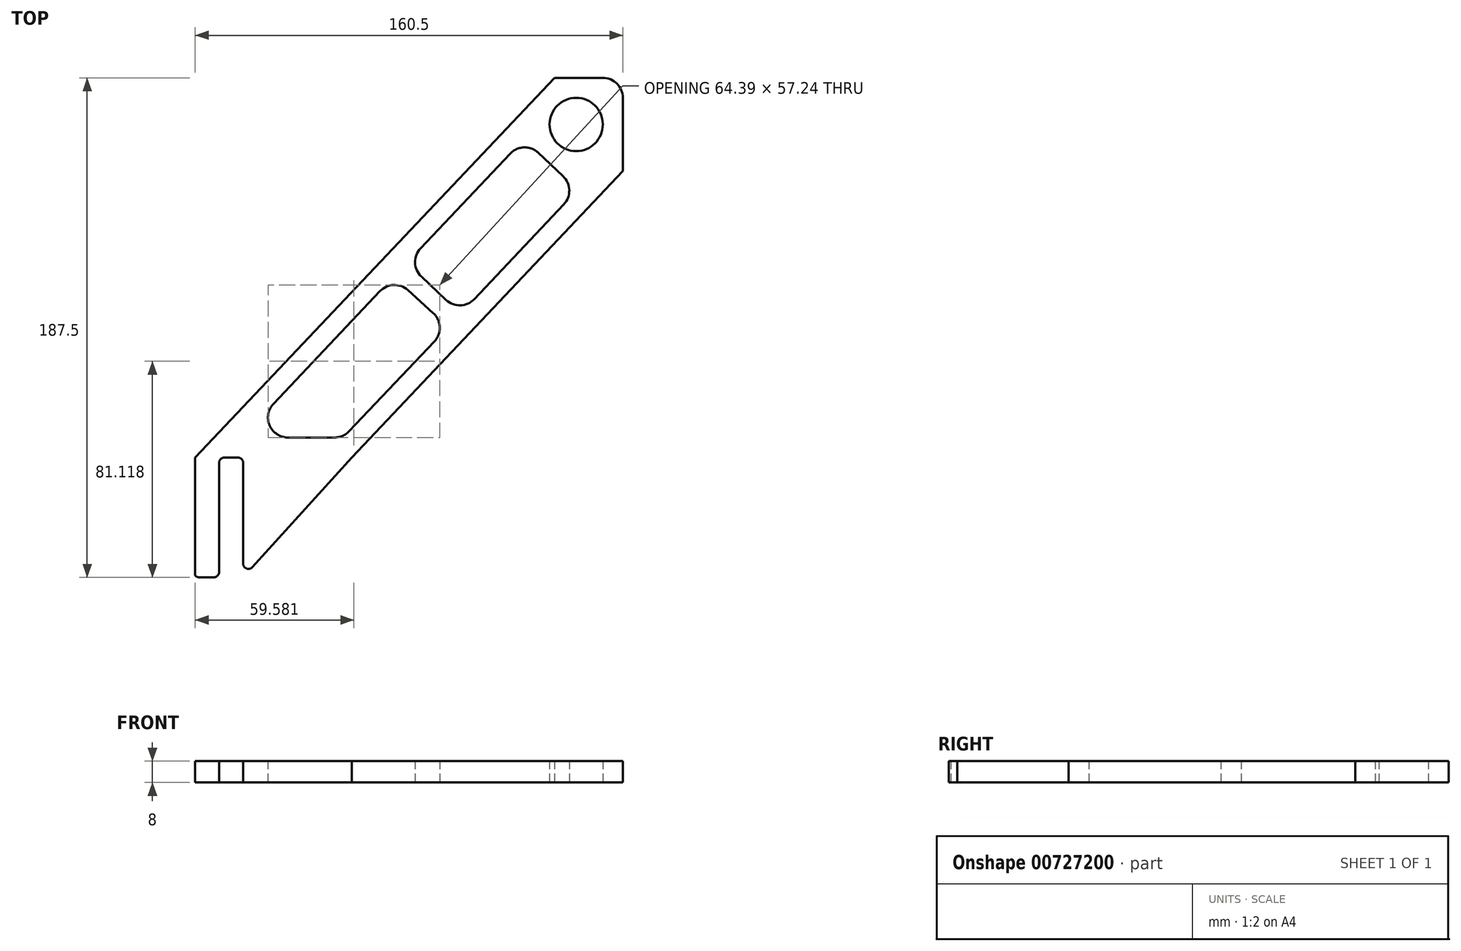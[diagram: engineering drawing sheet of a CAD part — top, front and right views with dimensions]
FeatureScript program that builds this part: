
annotation { "Feature Type Name" : "Feature", "Feature Type Description" : "" }
export const myFeature = defineFeature(function(context is Context, id is Id, definition is map)
    precondition{}
    {
        {
            var Q0;
            Q0=qCreatedBy(makeId("Top.planeOp"),FACE);
            var sketch = newSketch(context, id + "F0", { "sketchPlane" : qUnion([Q0])});
            skLineSegment(sketch, "E0", {"start": v(0, 0) * mm, "end": v(0, 125) * mm, "construction": true});
            skLineSegment(sketch, "E1", {"start": v(0, 125) * mm, "end": v(125, 125) * mm, "construction": true});
            skCircle(sketch, "E2", {"center": v(125, 125) * mm, "radius": 10 * mm});
            skLineSegment(sketch, "E3", {"start": v(0, -2) * mm, "end": v(0, -39.82) * mm});
            skLineSegment(sketch, "E4", {"start": v(-2, 0) * mm, "end": v(-7, 0) * mm});
            skLineSegment(sketch, "E5", {"start": v(-9, -2) * mm, "end": v(-9, -43) * mm});
            skLineSegment(sketch, "E6", {"start": v(-11, -45) * mm, "end": v(-16.47, -45) * mm});
            skLineSegment(sketch, "E7", {"start": v(125, 125) * mm, "end": v(112.62, 112.62) * mm, "construction": true});
            skLineSegment(sketch, "E8", {"start": v(142.5, 135) * mm, "end": v(142.5, 125) * mm});
            skLineSegment(sketch, "E9", {"start": v(125, 125) * mm, "end": v(185, 125) * mm, "construction": true});
            skLineSegment(sketch, "E10", {"start": v(142.5, 125) * mm, "end": v(142.5, 107.5) * mm});
            skLineSegment(sketch, "E11", {"start": v(116.8, 142.5) * mm, "end": v(104.78, 129.8) * mm});
            skLineSegment(sketch, "E12", {"start": v(135, 142.5) * mm, "end": v(116.8, 142.5) * mm});
            skLineSegment(sketch, "E13", {"start": v(142.5, 107.5) * mm, "end": v(130.93, 95.26) * mm});
            skLineSegment(sketch, "E14", {"start": v(40.81, 0) * mm, "end": v(3.48, -41.16) * mm});
            skLineSegment(sketch, "E15", {"start": v(-18, 0) * mm, "end": v(40.81, 0) * mm, "construction": true});
            skPoint(sketch, "E16.visualSharp", {"position": v(142.5, 142.5) * mm});
            skArc(sketch, "E16.filletArc", {"start": v(142.5, 135) * mm, "mid": v(140.3, 140.3) * mm, "end": v(135, 142.5) * mm});
            skPoint(sketch, "E17.visualSharp", {"position": v(-18, -45) * mm});
            skArc(sketch, "E17.filletArc", {"start": v(-18, -44.29) * mm, "mid": v(-17.31, -44.81) * mm, "end": v(-16.47, -45) * mm});
            skPoint(sketch, "E18.visualSharp", {"position": v(-9, -45) * mm});
            skArc(sketch, "E18.filletArc", {"start": v(-11, -45) * mm, "mid": v(-9.59, -44.41) * mm, "end": v(-9, -43) * mm});
            skPoint(sketch, "E19.visualSharp", {"position": v(-9, 0) * mm});
            skArc(sketch, "E19.filletArc", {"start": v(-7, 0) * mm, "mid": v(-8.41, -0.59) * mm, "end": v(-9, -2) * mm});
            skPoint(sketch, "E20.visualSharp", {"position": v(0, 0) * mm});
            skArc(sketch, "E20.filletArc", {"start": v(0, -2) * mm, "mid": v(-0.59, -0.59) * mm, "end": v(-2, 0) * mm});
            skPoint(sketch, "E21.visualSharp", {"position": v(0, -45) * mm});
            skArc(sketch, "E21.filletArc", {"start": v(0, -39.82) * mm, "mid": v(1.28, -41.68) * mm, "end": v(3.48, -41.16) * mm});
            skLineSegment(sketch, "E22", {"start": v(104.78, 129.8) * mm, "end": v(-18, 0) * mm});
            skLineSegment(sketch, "E23", {"start": v(40.81, 0) * mm, "end": v(40.81, 0) * mm});
            skLineSegment(sketch, "E24.0", {"start": v(16.84, 7.5) * mm, "end": v(34.35, 7.5) * mm});
            skLineSegment(sketch, "E25", {"start": v(130.93, 95.26) * mm, "end": v(130.93, 95.26) * mm});
            skLineSegment(sketch, "E26", {"start": v(130.93, 95.26) * mm, "end": v(40.81, 0) * mm});
            skLineSegment(sketch, "E27.0", {"start": v(120.34, 94.98) * mm, "end": v(86.72, 59.45) * mm});
            skLineSegment(sketch, "E28", {"start": v(37.58, 7.5) * mm, "end": v(37.58, 7.5) * mm});
            skLineSegment(sketch, "E29", {"start": v(110.81, 114.34) * mm, "end": v(120.05, 105.58) * mm});
            skLineSegment(sketch, "E30", {"start": v(100.2, 114.05) * mm, "end": v(66.58, 78.5) * mm});
            skPoint(sketch, "E31.visualSharp", {"position": v(125.48, 100.42) * mm});
            skArc(sketch, "E31.filletArc", {"start": v(120.34, 94.98) * mm, "mid": v(122.38, 100.34) * mm, "end": v(120.05, 105.58) * mm});
            skPoint(sketch, "E32.visualSharp", {"position": v(105.36, 119.5) * mm});
            skArc(sketch, "E32.filletArc", {"start": v(110.81, 114.34) * mm, "mid": v(105.45, 116.4) * mm, "end": v(100.2, 114.05) * mm});
            skPoint(sketch, "E33.visualSharp", {"position": v(-0.58, 7.5) * mm});
            skArc(sketch, "E33.filletArc", {"start": v(11.39, 20.15) * mm, "mid": v(9.95, 12.03) * mm, "end": v(16.84, 7.5) * mm});
            skPoint(sketch, "E34.visualSharp", {"position": v(37.58, 7.5) * mm});
            skArc(sketch, "E34.filletArc", {"start": v(34.35, 7.5) * mm, "mid": v(37.32, 8.11) * mm, "end": v(39.8, 9.85) * mm});
            skLineSegment(sketch, "E35", {"start": v(112.62, 112.62) * mm, "end": v(7.5, 7.5) * mm, "construction": true});
            skLineSegment(sketch, "E36", {"start": v(7.5, 7.5) * mm, "end": v(0, 0) * mm, "construction": true});
            skPoint(sketch, "E37.orphan", {"position": v(60.06, 60.06) * mm});
            skLineSegment(sketch, "E38.0.left", {"start": v(71.31, 54.23) * mm, "end": v(61.82, 62.8) * mm});
            skLineSegment(sketch, "E38.0.right", {"start": v(76.12, 59.15) * mm, "end": v(66.88, 67.9) * mm});
            skLineSegment(sketch, "E39", {"start": v(51.35, 62.4) * mm, "end": v(11.39, 20.15) * mm});
            skLineSegment(sketch, "E40", {"start": v(71.72, 43.5) * mm, "end": v(39.8, 9.85) * mm});
            skPoint(sketch, "E41.visualSharp", {"position": v(61.43, 73.05) * mm});
            skArc(sketch, "E41.filletArc", {"start": v(66.58, 78.5) * mm, "mid": v(64.53, 73.14) * mm, "end": v(66.88, 67.9) * mm});
            skPoint(sketch, "E42.visualSharp", {"position": v(81.57, 54) * mm});
            skArc(sketch, "E42.filletArc", {"start": v(76.12, 59.15) * mm, "mid": v(81.48, 57.1) * mm, "end": v(86.72, 59.45) * mm});
            skPoint(sketch, "E43.visualSharp", {"position": v(77, 49.08) * mm});
            skArc(sketch, "E43.filletArc", {"start": v(71.72, 43.5) * mm, "mid": v(73.78, 48.96) * mm, "end": v(71.31, 54.23) * mm});
            skPoint(sketch, "E44.visualSharp", {"position": v(56.38, 67.72) * mm});
            skArc(sketch, "E44.filletArc", {"start": v(61.82, 62.8) * mm, "mid": v(56.5, 64.74) * mm, "end": v(51.35, 62.4) * mm});
            skLineSegment(sketch, "E45", {"start": v(-18, -44.29) * mm, "end": v(-18, 0) * mm});
            skSolve(sketch);
        }
        {
            var Q0;
            Q0=makeQuery(id+"F0.imprint","IMPRINT",FACE,{"disambiguationData":[TD([[makeQuery(id+"F0.imprint","IMPRINT",EDGE,{"derivedFrom":sQuery(id+"F0.wireOp",EDGE,"E2")}),-1.0]])]});
            extrude(context, id + "F1", {"entities" : qUnion([Q0]), "depth" : 8 * mm, "offsetDistance" : 25 * mm});
        }
    });
